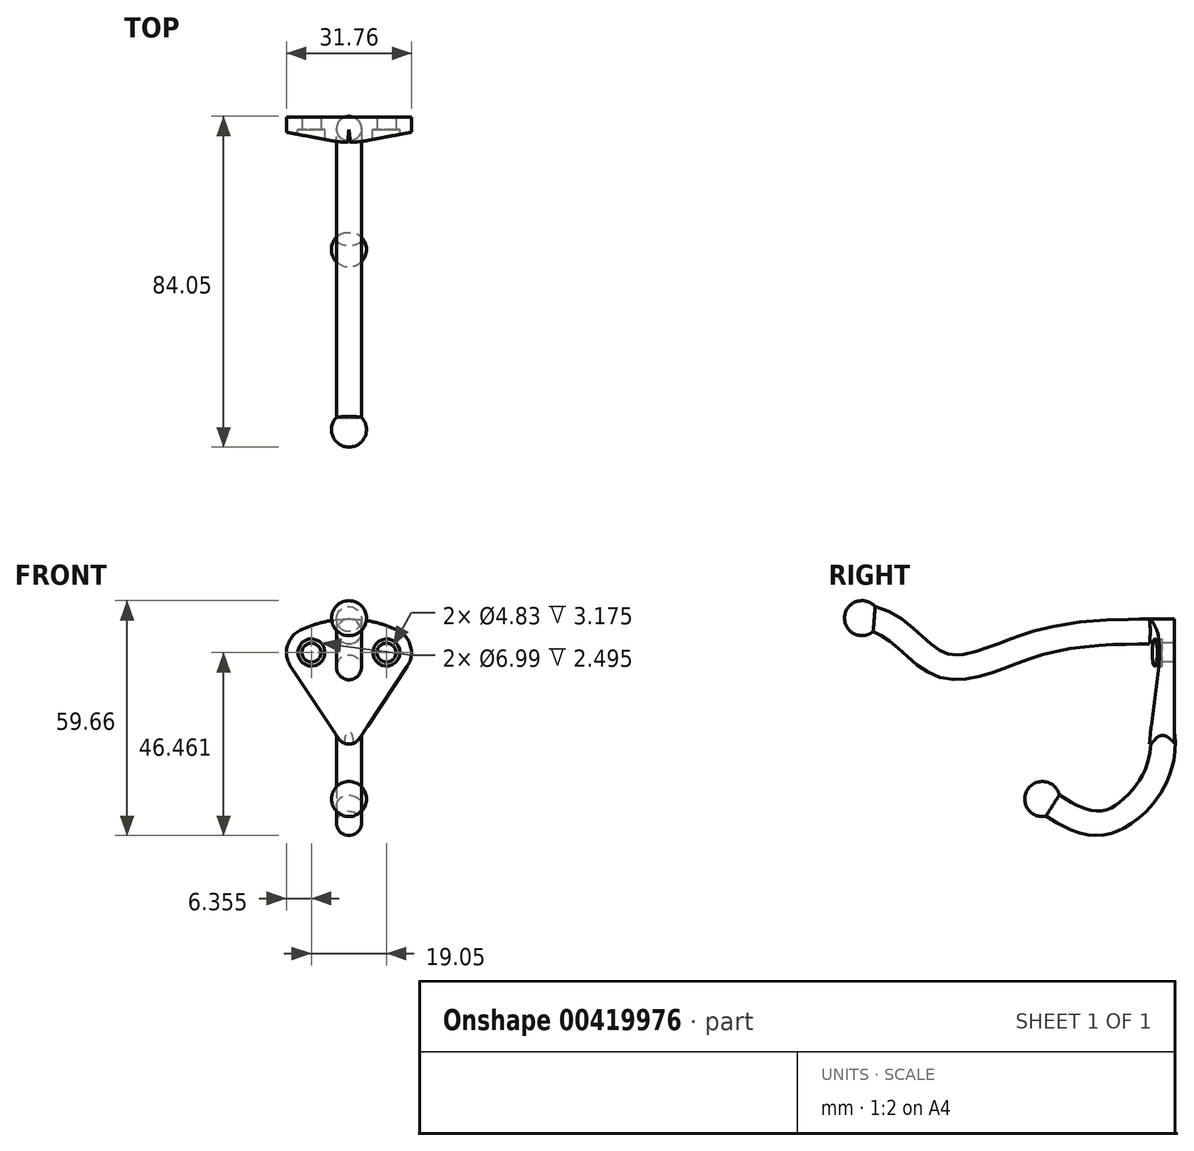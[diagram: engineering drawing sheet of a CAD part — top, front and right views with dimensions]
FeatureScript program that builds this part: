
annotation { "Feature Type Name" : "Feature", "Feature Type Description" : "" }
export const myFeature = defineFeature(function(context is Context, id is Id, definition is map)
    precondition{}
    {
        {
            var Q0;
            Q0=qCreatedBy(makeId("Front.planeOp"),FACE);
            var sketch = newSketch(context, id + "F0", { "sketchPlane" : qUnion([Q0])});
            skArc(sketch, "E0", {"start": v(12.25, 0.42) * mm, "mid": v(0, 3.17) * mm, "end": v(-12.25, 0.42) * mm});
            skArc(sketch, "E1", {"start": v(-2.64, -27.16) * mm, "mid": v(0, -28.58) * mm, "end": v(2.64, -27.16) * mm});
            skLineSegment(sketch, "E2", {"start": v(-2.64, -27.16) * mm, "end": v(-14.81, -8.83) * mm});
            skLineSegment(sketch, "E3", {"start": v(2.64, -27.16) * mm, "end": v(14.81, -8.83) * mm});
            skLineSegment(sketch, "E4", {"start": v(0, -25.4) * mm, "end": v(0, 0) * mm, "construction": true});
            skPoint(sketch, "E5.visualSharp", {"position": v(-18.36, -3.5) * mm});
            skArc(sketch, "E5.filletArc", {"start": v(-12.25, 0.42) * mm, "mid": v(-15.64, -3.62) * mm, "end": v(-14.81, -8.83) * mm});
            skPoint(sketch, "E6.visualSharp", {"position": v(18.36, -3.5) * mm});
            skArc(sketch, "E6.filletArc", {"start": v(14.81, -8.83) * mm, "mid": v(15.64, -3.62) * mm, "end": v(12.25, 0.42) * mm});
            skCircle(sketch, "E7", {"center": v(-9.52, -5.32) * mm, "radius": 2.41 * mm});
            skCircle(sketch, "E8", {"center": v(9.52, -5.32) * mm, "radius": 2.41 * mm});
            skSolve(sketch);
        }
        {
            var Q0;
            Q0 = qSketchRegion(id + "F0", true);
            extrude(context, id + "F1", {"entities" : qUnion([Q0]), "oppositeDirection" : true, "depth" : 6.35 * mm, "symmetric" : true});
        }
        {
            var Q0;
            Q0=qCreatedBy(makeId("Top.planeOp"),FACE);
            var sketch = newSketch(context, id + "F2", { "sketchPlane" : qUnion([Q0])});
            skLineSegment(sketch, "E9", {"start": v(-4.7, -2.74) * mm, "end": v(-15.88, -0.64) * mm});
            skLineSegment(sketch, "E10", {"start": v(-15.88, -0.63) * mm, "end": v(-15.88, -3.68) * mm});
            skLineSegment(sketch, "E11", {"start": v(-15.88, -3.68) * mm, "end": v(0, -3.68) * mm});
            skLineSegment(sketch, "E12", {"start": v(0, -3.68) * mm, "end": v(0, -3.62) * mm, "construction": true});
            skLineSegment(sketch, "E13.MirrorCS", {"start": v(4.7, -2.74) * mm, "end": v(15.88, -0.64) * mm});
            skLineSegment(sketch, "E14.MirrorCS", {"start": v(15.88, -0.63) * mm, "end": v(15.88, -3.68) * mm});
            skLineSegment(sketch, "E15.MirrorCS", {"start": v(15.88, -3.68) * mm, "end": v(0, -3.68) * mm});
            skPoint(sketch, "E16.visualSharp", {"position": v(0, -3.62) * mm});
            skArc(sketch, "E16.filletArc", {"start": v(-4.7, -2.74) * mm, "mid": v(0, -3.18) * mm, "end": v(4.7, -2.74) * mm});
            skSolve(sketch);
        }
        {
            var Q0;
            Q0 = qSketchRegion(id + "F2", true);
            extrude(context, id + "F3", {"entities" : qUnion([Q0]), "operationType" : NewBodyOperationType.REMOVE, "endBound" : BoundingType.THROUGH_ALL, "oppositeDirection" : true, "depth" : 25.4 * mm, "hasSecondDirection" : true, "secondDirectionBound" : BoundingType.THROUGH_ALL, "secondDirectionOppositeDirection" : false, "secondDirectionDepth" : 25.4 * mm});
        }
        {
            var Q0;
            Q0=qCreatedBy(makeId("Front.planeOp"),FACE);
            var sketch = newSketch(context, id + "F4", { "sketchPlane" : qUnion([Q0])});
            skCircle(sketch, "E17", {"center": v(-9.52, -5.32) * mm, "radius": 3.5 * mm});
            skCircle(sketch, "E18", {"center": v(9.52, -5.32) * mm, "radius": 3.5 * mm});
            skSolve(sketch);
        }
        {
            var Q0;
            Q0 = qSketchRegion(id + "F4", true);
            extrude(context, id + "F5", {"entities" : qUnion([Q0]), "operationType" : NewBodyOperationType.REMOVE, "endBound" : BoundingType.THROUGH_ALL, "depth" : 25.4 * mm});
        }
        {
            var Q0;
            Q0=qCreatedBy(makeId("Right.planeOp"),FACE);
            var sketch = newSketch(context, id + "F6", { "sketchPlane" : qUnion([Q0])});
            skFitSpline(sketch, "E19", {"points": [v(0, 0) * mm, v(-30.6, -2.62) * mm, v(-56.26, -8.33) * mm, v(-76.2, 3.43) * mm], "startDerivative": vector(-54.47, 0) * mm, "endDerivative": vector(-79.06, -6.87) * mm});
            skFitSpline(sketch, "E20", {"points": [v(0, -28.58) * mm, v(-14.22, -47.97) * mm, v(-33.11, -40.85) * mm], "startDerivative": vector(0, -55.11) * mm, "endDerivative": vector(-46.92, 29.05) * mm});
            skLineSegment(sketch, "E21", {"start": v(0, -28.58) * mm, "end": v(0, -25.4) * mm});
            skSolve(sketch);
        }
        {
            var Q0;
            Q0=qCreatedBy(makeId("Front.planeOp"),FACE);
            var sketch = newSketch(context, id + "F7", { "sketchPlane" : qUnion([Q0])});
            skCircle(sketch, "E22", {"center": v(0, 0) * mm, "radius": 3.18 * mm});
            skSolve(sketch);
        }
        {
            var Q0;
            Q0=makeQuery(id+"F7.imprint","IMPRINT",FACE,{"disambiguationData":[TD([[makeQuery(id+"F7.imprint","IMPRINT",EDGE,{"derivedFrom":sQuery(id+"F7.wireOp",EDGE,"E22")}),1.0]])]});
            var Q1;
            Q1=sQuery(id+"F6.wireOp",EDGE,"E19");
            sweep(context, id + "F8", {"operationType" : NewBodyOperationType.ADD, "profiles" : qUnion([Q0]), "path" : qUnion([Q1])});
        }
        {
            var Q0;
            Q0=qCreatedBy(makeId("Top.planeOp"),FACE);
            var Q1;
            Q1=sQuery(id+"F6.wireOp",VERTEX,"E21.end");
            cPlane(context, id + "F9", {"entities" : qUnion([Q0, Q1]), "cplaneType" : CPlaneType.PLANE_POINT, "offset" : 25.4 * mm, "width" : 152.4 * mm, "height" : 152.4 * mm});
        }
        {
            var Q0;
            Q0=qCreatedBy(id+"F9.planeOp",FACE);
            var sketch = newSketch(context, id + "F10", { "sketchPlane" : qUnion([Q0])});
            skCircle(sketch, "E23", {"center": v(0, 0) * mm, "radius": 3.18 * mm});
            skSolve(sketch);
        }
        {
            var Q0;
            Q0=makeQuery(id+"F10.imprint","IMPRINT",FACE,{"disambiguationData":[TD([[makeQuery(id+"F10.imprint","IMPRINT",EDGE,{"derivedFrom":sQuery(id+"F10.wireOp",EDGE,"E23")}),1.0]])]});
            var Q1;
            Q1=sQuery(id+"F6.wireOp",EDGE,"E20");
            sweep(context, id + "F11", {"operationType" : NewBodyOperationType.ADD, "profiles" : qUnion([Q0]), "path" : qUnion([Q1])});
        }
        {
            var Q0;
            Q0=makeQuery(id+"F11.opSweep","CAP_FACE",FACE,{"disambiguationData":[OSD([sQuery(id+"F6.wireOp",VERTEX,"E20.end"),sQuery(id+"F10.wireOp",EDGE,"E23")])],"isStart":false});
            var sketch = newSketch(context, id + "F12", { "sketchPlane" : qUnion([Q0])});
            skArc(sketch, "E24", {"start": v(0, -56.6) * mm, "mid": v(4.45, -52.16) * mm, "end": v(0, -47.72) * mm});
            skLineSegment(sketch, "E25", {"start": v(0, -47.72) * mm, "end": v(0, -56.6) * mm});
            skLineSegment(sketch, "E26", {"start": v(0, -56.6) * mm, "end": v(0, -65.2) * mm, "construction": true});
            skSolve(sketch);
        }
        {
            var Q0;
            Q0 = qSketchRegion(id + "F12", true);
            var Q1;
            Q1=sQuery(id+"F12.wireOp",EDGE,"E26");
            revolve(context, id + "F13", {"operationType" : NewBodyOperationType.ADD, "entities" : qUnion([Q0]), "axis" : qUnion([Q1]), "revolveType" : RevolveType.FULL});
        }
        {
            var Q0;
            Q0=makeQuery(id+"F8.opSweep","CAP_FACE",FACE,{"disambiguationData":[OSD([sQuery(id+"F6.wireOp",VERTEX,"E19.end"),sQuery(id+"F7.wireOp",EDGE,"E22")])],"isStart":false});
            var sketch = newSketch(context, id + "F14", { "sketchPlane" : qUnion([Q0])});
            skArc(sketch, "E27", {"start": v(0, 5.58) * mm, "mid": v(4.45, 10.02) * mm, "end": v(0, 14.47) * mm});
            skLineSegment(sketch, "E28", {"start": v(0, 14.47) * mm, "end": v(0, 5.58) * mm});
            skLineSegment(sketch, "E29", {"start": v(0, 5.58) * mm, "end": v(0, -4.3) * mm, "construction": true});
            skSolve(sketch);
        }
        {
            var Q0;
            Q0 = qSketchRegion(id + "F14", true);
            var Q1;
            Q1=sQuery(id+"F14.wireOp",EDGE,"E29");
            revolve(context, id + "F15", {"operationType" : NewBodyOperationType.ADD, "entities" : qUnion([Q0]), "axis" : qUnion([Q1]), "revolveType" : RevolveType.FULL});
        }
    });
